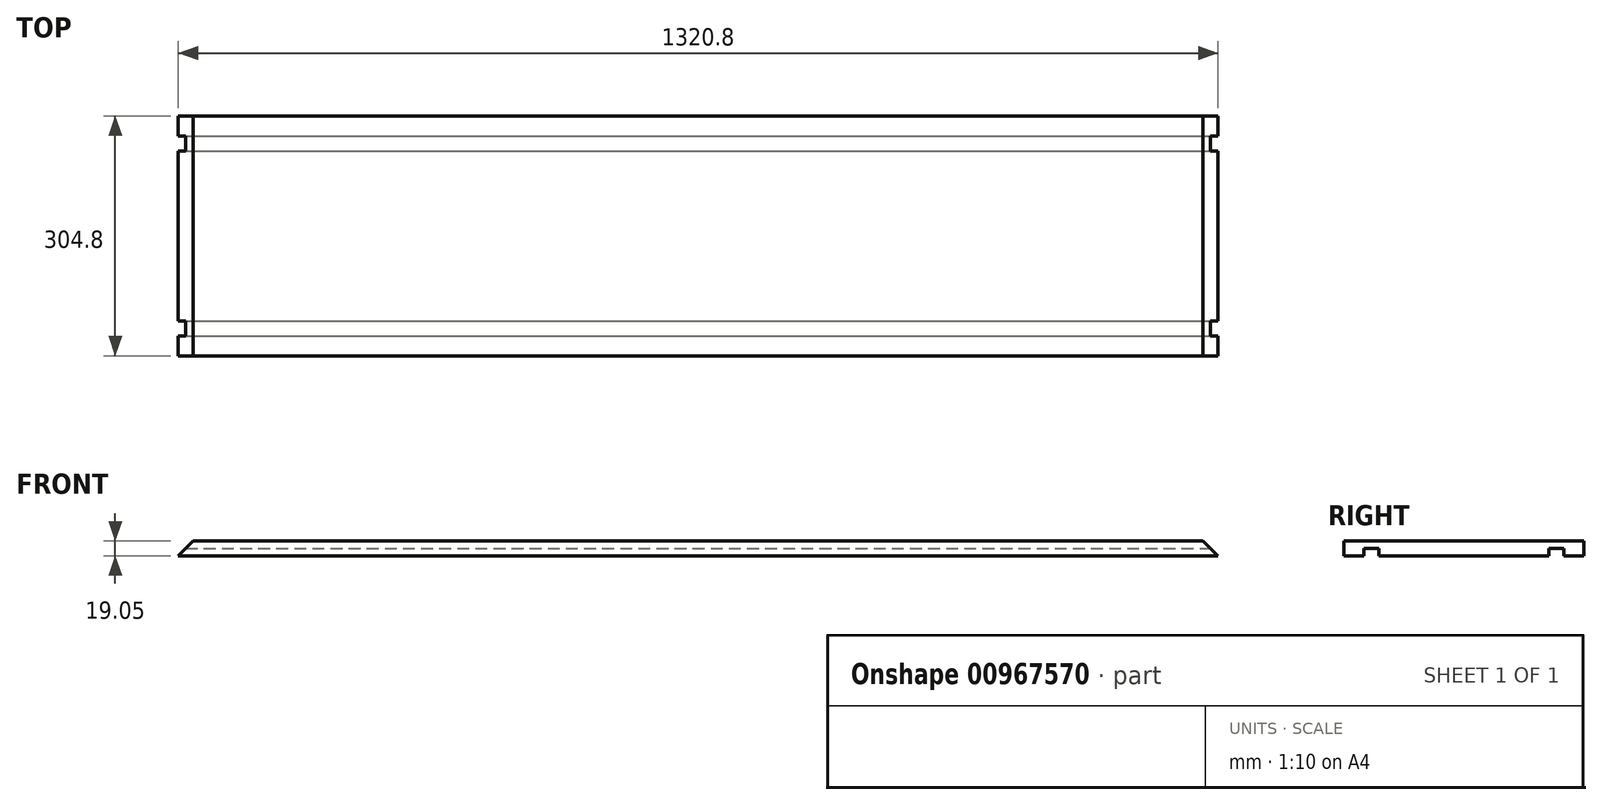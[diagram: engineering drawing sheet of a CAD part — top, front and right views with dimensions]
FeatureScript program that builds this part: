
annotation { "Feature Type Name" : "Feature", "Feature Type Description" : "" }
export const myFeature = defineFeature(function(context is Context, id is Id, definition is map)
    precondition{}
    {
        {
            var Q0;
            Q0=qCreatedBy(makeId("Top.planeOp"),FACE);
            var sketch = newSketch(context, id + "F0", { "sketchPlane" : qUnion([Q0])});
            skLineSegment(sketch, "E0.bottom", {"start": v(-613.05, 59.9) * mm, "end": v(707.75, 59.9) * mm});
            skLineSegment(sketch, "E0.top", {"start": v(-613.05, -244.9) * mm, "end": v(707.75, -244.9) * mm});
            skLineSegment(sketch, "E0.left", {"start": v(-613.05, 59.9) * mm, "end": v(-613.05, -244.9) * mm});
            skLineSegment(sketch, "E0.right", {"start": v(707.75, 59.9) * mm, "end": v(707.75, -244.9) * mm});
            skSolve(sketch);
        }
        {
            var Q0;
            Q0=makeQuery(id+"F0.imprint","IMPRINT",FACE,{"disambiguationData":[TD([[makeQuery(id+"F0.imprint","IMPRINT",EDGE,{"derivedFrom":sQuery(id+"F0.wireOp",EDGE,"E0.bottom")}),-1.0]])]});
            extrude(context, id + "F1", {"entities" : qUnion([Q0]), "depth" : 19.05 * mm, "offsetDistance" : 25.4 * mm});
        }
        {
            var Q0;
            Q0=makeQuery(id+"F1.opExtrude","CAP_EDGE",EDGE,{"disambiguationData":[OSD([sQuery(id+"F0.wireOp",EDGE,"E0.right")])],"isStart":false});
            var Q1;
            Q1=makeQuery(id+"F1.opExtrude","CAP_EDGE",EDGE,{"disambiguationData":[OSD([sQuery(id+"F0.wireOp",EDGE,"E0.left")])],"isStart":false});
            chamfer(context, id + "F2", {"entities" : qUnion([Q0, Q1]), "width" : 19.05 * mm});
        }
        {
            var Q0;
            Q0=makeQuery(id+"F1.opExtrude","CAP_FACE",FACE,{"disambiguationData":[OSD([sQuery(id+"F0.wireOp",EDGE,"E0.bottom"),sQuery(id+"F0.wireOp",EDGE,"E0.top"),sQuery(id+"F0.wireOp",EDGE,"E0.left"),sQuery(id+"F0.wireOp",EDGE,"E0.right")])],"isStart":true});
            var sketch = newSketch(context, id + "F3", { "sketchPlane" : qUnion([Q0])});
            skLineSegment(sketch, "E1.bottom", {"start": v(-613.05, 219.5) * mm, "end": v(707.75, 219.5) * mm});
            skLineSegment(sketch, "E1.top", {"start": v(-613.05, 200.45) * mm, "end": v(707.75, 200.45) * mm});
            skLineSegment(sketch, "E1.left", {"start": v(-613.05, 219.5) * mm, "end": v(-613.05, 200.45) * mm});
            skLineSegment(sketch, "E1.right", {"start": v(707.75, 219.5) * mm, "end": v(707.75, 200.45) * mm});
            skLineSegment(sketch, "E2.bottom", {"start": v(-613.05, -34.5) * mm, "end": v(707.75, -34.5) * mm});
            skLineSegment(sketch, "E2.top", {"start": v(-613.05, -15.45) * mm, "end": v(707.75, -15.45) * mm});
            skLineSegment(sketch, "E2.left", {"start": v(-613.05, -34.5) * mm, "end": v(-613.05, -15.45) * mm});
            skLineSegment(sketch, "E2.right", {"start": v(707.75, -34.5) * mm, "end": v(707.75, -15.45) * mm});
            skSolve(sketch);
        }
        {
            var Q0;
            Q0=makeQuery(id+"F3.imprint","IMPRINT",FACE,{"disambiguationData":[TD([[makeQuery(id+"F3.imprint","IMPRINT",EDGE,{"derivedFrom":sQuery(id+"F3.wireOp",EDGE,"E1.bottom")}),-1.0]])]});
            var Q1;
            Q1=makeQuery(id+"F3.imprint","IMPRINT",FACE,{"disambiguationData":[TD([[makeQuery(id+"F3.imprint","IMPRINT",EDGE,{"derivedFrom":sQuery(id+"F3.wireOp",EDGE,"E2.bottom")}),1.0]])]});
            extrude(context, id + "F4", {"entities" : qUnion([Q0, Q1]), "operationType" : NewBodyOperationType.REMOVE, "oppositeDirection" : true, "depth" : 9.52 * mm, "offsetDistance" : 25.4 * mm});
        }
    });
